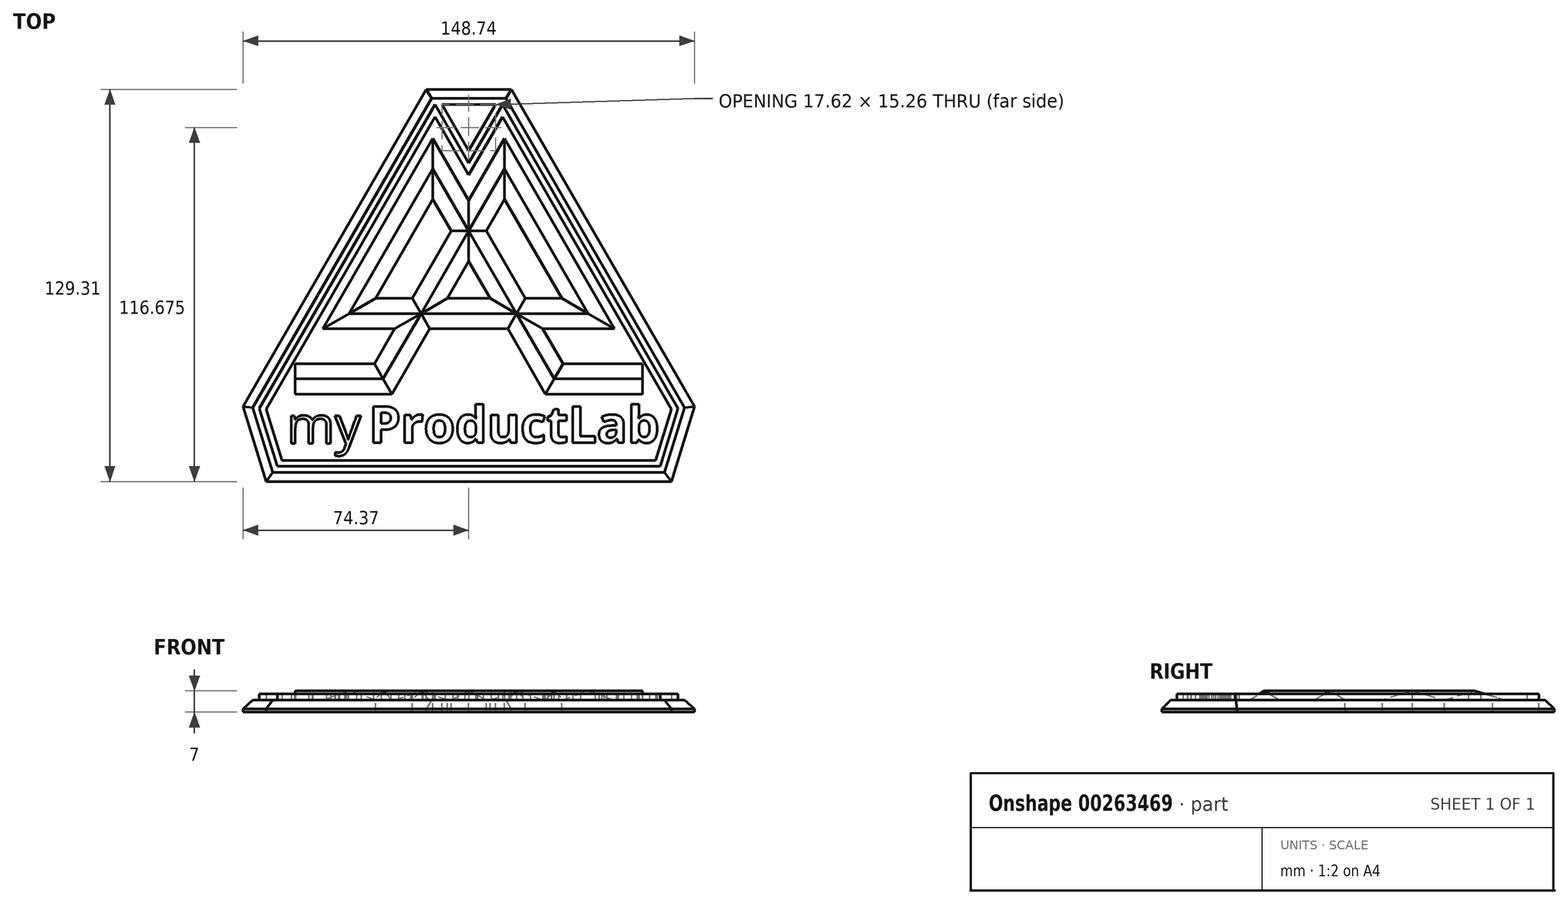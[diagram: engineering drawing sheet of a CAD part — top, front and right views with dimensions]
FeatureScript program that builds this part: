
annotation { "Feature Type Name" : "Feature", "Feature Type Description" : "" }
export const myFeature = defineFeature(function(context is Context, id is Id, definition is map)
    precondition{}
    {
        {
            var Q0;
            Q0=qCreatedBy(makeId("Top.planeOp"),FACE);
            var sketch = newSketch(context, id + "F0", { "sketchPlane" : qUnion([Q0])});
            skLineSegment(sketch, "E0", {"start": v(11.81, 20.46) * mm, "end": v(39.36, -27.25) * mm});
            skLineSegment(sketch, "E1", {"start": v(-39.36, -27.25) * mm, "end": v(-11.81, 20.46) * mm});
            skLineSegment(sketch, "E2", {"start": v(-11.81, 20.46) * mm, "end": v(28.18, -48.8) * mm});
            skLineSegment(sketch, "E3", {"start": v(28.18, -48.8) * mm, "end": v(57.26, -48.8) * mm});
            skLineSegment(sketch, "E4", {"start": v(-28.18, -48.8) * mm, "end": v(-57.26, -48.8) * mm});
            skLineSegment(sketch, "E5", {"start": v(-28.18, -48.8) * mm, "end": v(11.81, 20.46) * mm});
            skLineSegment(sketch, "E6", {"start": v(-39.36, -27.25) * mm, "end": v(0, -27.25) * mm});
            skLineSegment(sketch, "E7", {"start": v(0, -27.25) * mm, "end": v(39.36, -27.25) * mm});
            skSolve(sketch);
        }
        {
            var Q0;
            Q0=sQuery(id+"F0.wireOp",VERTEX,"E4.end");
            var Q1;
            Q1=sQuery(id+"F0.wireOp",EDGE,"E4");
            cPlane(context, id + "F1", {"entities" : qUnion([Q0, Q1]), "cplaneType" : CPlaneType.LINE_POINT, "offset" : 25 * mm, "width" : 150 * mm, "height" : 150 * mm});
        }
        {
            var Q0;
            Q0=qCreatedBy(id+"F1.planeOp",FACE);
            var sketch = newSketch(context, id + "F2", { "sketchPlane" : qUnion([Q0])});
            skLineSegment(sketch, "E8", {"start": v(48.8, 0) * mm, "end": v(43.8, -3) * mm});
            skLineSegment(sketch, "E9", {"start": v(43.8, -3) * mm, "end": v(53.8, -3) * mm});
            skLineSegment(sketch, "E10", {"start": v(53.8, -3) * mm, "end": v(48.8, 0) * mm});
            skSolve(sketch);
        }
        {
            var Q0;
            Q0 = qSketchRegion(id + "F2", true);
            var Q1;
            Q1=sQuery(id+"F0.wireOp",EDGE,"E4");
            var Q2;
            Q2=sQuery(id+"F0.wireOp",EDGE,"E5");
            var Q3;
            Q3=sQuery(id+"F0.wireOp",EDGE,"E0");
            var Q4;
            Q4=sQuery(id+"F0.wireOp",EDGE,"E7");
            sweep(context, id + "F3", {"profiles" : qUnion([Q0]), "path" : qUnion([Q1, Q2, Q3, Q4])});
        }
        {
            var Q0;
            Q0=makeQuery(id+"F3.opSweep","SWEPT_BODY",BODY,{"disambiguationData":[OSD([sQuery(id+"F0.wireOp",EDGE,"E7"),sQuery(id+"F2.wireOp",EDGE,"E8"),sQuery(id+"F2.wireOp",EDGE,"E9"),sQuery(id+"F2.wireOp",EDGE,"E10")])]});
            var Q1;
            Q1=qCreatedBy(makeId("Right.planeOp"),FACE);
            mirror(context, id + "F4", {"operationType" : NewBodyOperationType.ADD, "entities" : qUnion([Q0]), "mirrorPlane" : qUnion([Q1])});
        }
        {
            var Q0;
            {var subQ0=makeQuery(id+"F3.opSweep","SWEPT_FACE",FACE,{"disambiguationData":[OSD([sQuery(id+"F0.wireOp",EDGE,"E4"),sQuery(id+"F2.wireOp",EDGE,"E9")])]});Q0=makeQuery(id+"F4.boolean.opBoolean","MERGE",FACE,{"derivedFrom":[subQ0,makeQuery(id+"F4.opPattern","COPY",FACE,{"derivedFrom":subQ0,"instanceName":"1"})]});}
            var sketch = newSketch(context, id + "F5", { "sketchPlane" : qUnion([Q0])});
            skLineSegment(sketch, "E11", {"start": v(-74.37, 57.89) * mm, "end": v(-14, -46.67) * mm});
            skLineSegment(sketch, "E12", {"start": v(-74.37, 57.89) * mm, "end": v(-66.72, 82.64) * mm});
            skLineSegment(sketch, "E13", {"start": v(-66.72, 82.64) * mm, "end": v(0, 82.64) * mm});
            skLineSegment(sketch, "E14.MirrorCS", {"start": v(74.37, 57.89) * mm, "end": v(14, -46.67) * mm});
            skLineSegment(sketch, "E15.MirrorCS", {"start": v(74.37, 57.89) * mm, "end": v(66.72, 82.64) * mm});
            skLineSegment(sketch, "E16.MirrorCS", {"start": v(66.72, 82.64) * mm, "end": v(0, 82.64) * mm});
            skLineSegment(sketch, "E17", {"start": v(-14, -46.67) * mm, "end": v(14, -46.67) * mm});
            skPoint(sketch, "E18.orphan", {"position": v(0, -70.93) * mm});
            skSolve(sketch);
        }
        {
            var Q0;
            Q0 = qSketchRegion(id + "F5", true);
            extrude(context, id + "F6", {"entities" : qUnion([Q0]), "operationType" : NewBodyOperationType.ADD, "depth" : 4 * mm});
        }
        {
            var Q0;
            {var subQ0=sQuery(id+"F2.wireOp",EDGE,"E8");var subQ1=makeQuery(id+"F3.opSweep","SWEPT_FACE",FACE,{"disambiguationData":[OSD([sQuery(id+"F0.wireOp",EDGE,"E0"),subQ0])]});var subQ2=makeQuery(id+"F3.opSweep","SWEPT_FACE",FACE,{"disambiguationData":[OSD([sQuery(id+"F0.wireOp",EDGE,"E7"),subQ0])]});var subQ3=sQuery(id+"F0.wireOp",EDGE,"E5");var subQ4=makeQuery(id+"F3.opSweep","SWEPT_FACE",FACE,{"disambiguationData":[OSD([subQ3,subQ0])]});var subQ5=sQuery(id+"F5.wireOp",EDGE,"E11");var subQ6=sQuery(id+"F2.wireOp",EDGE,"E10");var subQ7=makeQuery(id+"F3.opSweep","SWEPT_FACE",FACE,{"disambiguationData":[OSD([subQ3,subQ6])]});var subQ8=sQuery(id+"F5.wireOp",EDGE,"E14.MirrorCS");var subQ9=makeQuery(id+"F3.opSweep","CAP_FACE",FACE,{"disambiguationData":[OSD([sQuery(id+"F0.wireOp",VERTEX,"E4.end"),subQ0,sQuery(id+"F2.wireOp",EDGE,"E9"),subQ6])],"isStart":true});var subQ10=sQuery(id+"F0.wireOp",EDGE,"E4");var subQ11=makeQuery(id+"F3.opSweep","SWEPT_FACE",FACE,{"disambiguationData":[OSD([subQ10,subQ0])]});var subQ12=makeQuery(id+"F3.opSweep","SWEPT_FACE",FACE,{"disambiguationData":[OSD([subQ10,subQ6])]});var subQ13=sQuery(id+"F5.wireOp",EDGE,"E17");var subQ14=sQuery(id+"F5.wireOp",EDGE,"E12");var subQ15=sQuery(id+"F5.wireOp",EDGE,"E16.MirrorCS");var subQ16=sQuery(id+"F5.wireOp",EDGE,"E13");var subQ17=sQuery(id+"F5.wireOp",EDGE,"E15.MirrorCS");Q0=makeQuery(id+"F6.boolean.opBoolean","SPLIT",FACE,{"disambiguationData":[TD([subQ9,subQ1,subQ11,subQ12,subQ4,subQ7,subQ2,makeQuery(id+"F4.opPattern","COPY",FACE,{"derivedFrom":subQ9,"instanceName":"1"}),makeQuery(id+"F4.opPattern","COPY",FACE,{"derivedFrom":subQ1,"instanceName":"1"}),makeQuery(id+"F4.opPattern","COPY",FACE,{"derivedFrom":subQ11,"instanceName":"1"}),makeQuery(id+"F4.opPattern","COPY",FACE,{"derivedFrom":subQ12,"instanceName":"1"}),makeQuery(id+"F4.opPattern","COPY",FACE,{"derivedFrom":subQ4,"instanceName":"1"}),makeQuery(id+"F4.opPattern","COPY",FACE,{"derivedFrom":subQ7,"instanceName":"1"}),makeQuery(id+"F4.opPattern","COPY",FACE,{"derivedFrom":subQ2,"instanceName":"1"}),makeQuery(id+"F6.opExtrude","SWEPT_FACE",FACE,{"disambiguationData":[OSD([subQ5])]}),makeQuery(id+"F6.opExtrude","SWEPT_FACE",FACE,{"disambiguationData":[OSD([subQ14])]}),makeQuery(id+"F6.opExtrude","SWEPT_FACE",FACE,{"disambiguationData":[OSD([subQ16,subQ15])]}),makeQuery(id+"F6.opExtrude","SWEPT_FACE",FACE,{"disambiguationData":[OSD([subQ8])]}),makeQuery(id+"F6.opExtrude","SWEPT_FACE",FACE,{"disambiguationData":[OSD([subQ17])]}),makeQuery(id+"F6.opExtrude","SWEPT_FACE",FACE,{"disambiguationData":[OSD([subQ13])]})])],"derivedFrom":makeQuery(id+"F6.opExtrude","CAP_FACE",FACE,{"disambiguationData":[OSD([subQ5,subQ14,subQ16,subQ8,subQ17,subQ15,subQ13])],"isStart":true})});}
            var sketch = newSketch(context, id + "F7", { "sketchPlane" : qUnion([Q0])});
            skLineSegment(sketch, "E19.0", {"start": v(-68.95, -58.5) * mm, "end": v(-11.12, 41.67) * mm});
            skLineSegment(sketch, "E19.1", {"start": v(68.95, -58.5) * mm, "end": v(11.12, 41.67) * mm});
            skLineSegment(sketch, "E19.2", {"start": v(68.95, -58.5) * mm, "end": v(63.03, -77.64) * mm});
            skLineSegment(sketch, "E19.3", {"start": v(63.03, -77.64) * mm, "end": v(-63.03, -77.64) * mm});
            skLineSegment(sketch, "E19.4", {"start": v(-68.95, -58.5) * mm, "end": v(-63.03, -77.64) * mm});
            skLineSegment(sketch, "E20", {"start": v(-11.12, 41.67) * mm, "end": v(0, 22.4) * mm});
            skLineSegment(sketch, "E21", {"start": v(0, 22.4) * mm, "end": v(11.12, 41.67) * mm});
            skLineSegment(sketch, "E22.0", {"start": v(-11.12, 37.67) * mm, "end": v(0, 18.4) * mm});
            skLineSegment(sketch, "E22.1", {"start": v(-66.78, -58.74) * mm, "end": v(-11.12, 37.67) * mm});
            skLineSegment(sketch, "E22.2", {"start": v(66.78, -58.74) * mm, "end": v(11.12, 37.67) * mm});
            skLineSegment(sketch, "E22.3", {"start": v(66.78, -58.74) * mm, "end": v(61.55, -75.64) * mm});
            skLineSegment(sketch, "E22.4", {"start": v(61.55, -75.64) * mm, "end": v(-61.55, -75.64) * mm});
            skLineSegment(sketch, "E22.5", {"start": v(0, 18.4) * mm, "end": v(11.12, 37.67) * mm});
            skLineSegment(sketch, "E22.6", {"start": v(-66.78, -58.74) * mm, "end": v(-61.55, -75.64) * mm});
            skSolve(sketch);
        }
        {
            var Q0;
            Q0 = qSketchRegion(id + "F7", true);
            extrude(context, id + "F8", {"entities" : qUnion([Q0]), "operationType" : NewBodyOperationType.ADD, "depth" : 2 * mm});
        }
        {
            var Q0;
            Q0=makeQuery(id+"F6.opExtrude","CAP_EDGE",EDGE,{"disambiguationData":[OSD([sQuery(id+"F5.wireOp",EDGE,"E17")])],"isStart":true});
            var Q1;
            Q1=makeQuery(id+"F6.opExtrude","CAP_EDGE",EDGE,{"disambiguationData":[OSD([sQuery(id+"F5.wireOp",EDGE,"E11")])],"isStart":true});
            var Q2;
            Q2=makeQuery(id+"F6.opExtrude","CAP_EDGE",EDGE,{"disambiguationData":[OSD([sQuery(id+"F5.wireOp",EDGE,"E14.MirrorCS")])],"isStart":true});
            var Q3;
            Q3=makeQuery(id+"F6.opExtrude","CAP_EDGE",EDGE,{"disambiguationData":[OSD([sQuery(id+"F5.wireOp",EDGE,"E15.MirrorCS")])],"isStart":true});
            var Q4;
            Q4=makeQuery(id+"F6.opExtrude","CAP_EDGE",EDGE,{"disambiguationData":[OSD([sQuery(id+"F5.wireOp",EDGE,"E13"),sQuery(id+"F5.wireOp",EDGE,"E16.MirrorCS")])],"isStart":true});
            var Q5;
            Q5=makeQuery(id+"F6.opExtrude","CAP_EDGE",EDGE,{"disambiguationData":[OSD([sQuery(id+"F5.wireOp",EDGE,"E12")])],"isStart":true});
            chamfer(context, id + "F9", {"entities" : qUnion([Q0, Q1, Q2, Q3, Q4, Q5]), "width" : 3 * mm, "tangentPropagation" : true});
        }
        {
            var Q0;
            {var subQ0=sQuery(id+"F5.wireOp",EDGE,"E17");var subQ1=makeQuery(id+"F6.opExtrude","SWEPT_FACE",FACE,{"disambiguationData":[OSD([subQ0])]});var subQ2=sQuery(id+"F5.wireOp",EDGE,"E15.MirrorCS");var subQ3=makeQuery(id+"F6.opExtrude","SWEPT_FACE",FACE,{"disambiguationData":[OSD([subQ2])]});var subQ4=sQuery(id+"F5.wireOp",EDGE,"E16.MirrorCS");var subQ5=sQuery(id+"F5.wireOp",EDGE,"E13");var subQ6=makeQuery(id+"F6.opExtrude","SWEPT_FACE",FACE,{"disambiguationData":[OSD([subQ5,subQ4])]});var subQ7=sQuery(id+"F5.wireOp",EDGE,"E12");var subQ8=makeQuery(id+"F6.opExtrude","SWEPT_FACE",FACE,{"disambiguationData":[OSD([subQ7])]});var subQ9=sQuery(id+"F5.wireOp",EDGE,"E11");var subQ10=makeQuery(id+"F6.opExtrude","SWEPT_FACE",FACE,{"disambiguationData":[OSD([subQ9])]});var subQ11=sQuery(id+"F5.wireOp",EDGE,"E14.MirrorCS");var subQ12=makeQuery(id+"F6.opExtrude","SWEPT_FACE",FACE,{"disambiguationData":[OSD([subQ11])]});var subQ13=sQuery(id+"F2.wireOp",EDGE,"E8");var subQ14=makeQuery(id+"F3.opSweep","SWEPT_FACE",FACE,{"disambiguationData":[OSD([sQuery(id+"F0.wireOp",EDGE,"E0"),subQ13])]});var subQ15=makeQuery(id+"F3.opSweep","SWEPT_FACE",FACE,{"disambiguationData":[OSD([sQuery(id+"F0.wireOp",EDGE,"E7"),subQ13])]});var subQ16=sQuery(id+"F0.wireOp",EDGE,"E5");var subQ17=makeQuery(id+"F3.opSweep","SWEPT_FACE",FACE,{"disambiguationData":[OSD([subQ16,subQ13])]});var subQ18=sQuery(id+"F2.wireOp",EDGE,"E10");var subQ19=makeQuery(id+"F3.opSweep","SWEPT_FACE",FACE,{"disambiguationData":[OSD([subQ16,subQ18])]});var subQ20=makeQuery(id+"F3.opSweep","CAP_FACE",FACE,{"disambiguationData":[OSD([sQuery(id+"F0.wireOp",VERTEX,"E4.end"),subQ13,sQuery(id+"F2.wireOp",EDGE,"E9"),subQ18])],"isStart":true});var subQ21=sQuery(id+"F0.wireOp",EDGE,"E4");var subQ22=makeQuery(id+"F3.opSweep","SWEPT_FACE",FACE,{"disambiguationData":[OSD([subQ21,subQ13])]});var subQ23=makeQuery(id+"F3.opSweep","SWEPT_FACE",FACE,{"disambiguationData":[OSD([subQ21,subQ18])]});Q0=makeQuery(id+"F8.boolean.opBoolean","SPLIT",FACE,{"disambiguationData":[TD([subQ10])],"derivedFrom":makeQuery(id+"F6.boolean.opBoolean","SPLIT",FACE,{"disambiguationData":[TD([subQ20,subQ14,subQ22,subQ23,subQ17,subQ19,subQ15,makeQuery(id+"F4.opPattern","COPY",FACE,{"derivedFrom":subQ20,"instanceName":"1"}),makeQuery(id+"F4.opPattern","COPY",FACE,{"derivedFrom":subQ14,"instanceName":"1"}),makeQuery(id+"F4.opPattern","COPY",FACE,{"derivedFrom":subQ22,"instanceName":"1"}),makeQuery(id+"F4.opPattern","COPY",FACE,{"derivedFrom":subQ23,"instanceName":"1"}),makeQuery(id+"F4.opPattern","COPY",FACE,{"derivedFrom":subQ17,"instanceName":"1"}),makeQuery(id+"F4.opPattern","COPY",FACE,{"derivedFrom":subQ19,"instanceName":"1"}),makeQuery(id+"F4.opPattern","COPY",FACE,{"derivedFrom":subQ15,"instanceName":"1"}),subQ10,subQ8,subQ6,subQ12,subQ3,subQ1])],"derivedFrom":makeQuery(id+"F6.opExtrude","CAP_FACE",FACE,{"disambiguationData":[OSD([subQ9,subQ7,subQ5,subQ11,subQ2,subQ4,subQ0])],"isStart":true})})});}
            var sketch = newSketch(context, id + "F10", { "sketchPlane" : qUnion([Q0])});
            skPoint(sketch, "E23", {"position": v(0, 43.67) * mm});
            skLineSegment(sketch, "E24", {"start": v(0, 26.4) * mm, "end": v(-8.81, 41.67) * mm});
            skLineSegment(sketch, "E25", {"start": v(-8.81, 41.67) * mm, "end": v(8.81, 41.67) * mm});
            skLineSegment(sketch, "E26", {"start": v(8.81, 41.67) * mm, "end": v(0, 26.4) * mm});
            skSolve(sketch);
        }
        {
            var Q0;
            Q0 = qSketchRegion(id + "F10", true);
            extrude(context, id + "F11", {"entities" : qUnion([Q0]), "operationType" : NewBodyOperationType.REMOVE, "oppositeDirection" : true, "depth" : 25 * mm});
        }
        {
            var Q0;
            {var subQ0=sQuery(id+"F2.wireOp",EDGE,"E8");var subQ1=makeQuery(id+"F3.opSweep","SWEPT_FACE",FACE,{"disambiguationData":[OSD([sQuery(id+"F0.wireOp",EDGE,"E0"),subQ0])]});var subQ2=makeQuery(id+"F4.opPattern","COPY",FACE,{"derivedFrom":subQ1,"instanceName":"1"});var subQ3=makeQuery(id+"F3.opSweep","SWEPT_FACE",FACE,{"disambiguationData":[OSD([sQuery(id+"F0.wireOp",EDGE,"E7"),subQ0])]});var subQ4=sQuery(id+"F0.wireOp",EDGE,"E5");var subQ5=makeQuery(id+"F3.opSweep","SWEPT_FACE",FACE,{"disambiguationData":[OSD([subQ4,subQ0])]});var subQ6=makeQuery(id+"F4.opPattern","COPY",FACE,{"derivedFrom":subQ5,"instanceName":"1"});var subQ7=sQuery(id+"F2.wireOp",EDGE,"E10");var subQ8=makeQuery(id+"F3.opSweep","SWEPT_FACE",FACE,{"disambiguationData":[OSD([subQ4,subQ7])]});var subQ9=makeQuery(id+"F3.opSweep","CAP_FACE",FACE,{"disambiguationData":[OSD([sQuery(id+"F0.wireOp",VERTEX,"E4.end"),subQ0,sQuery(id+"F2.wireOp",EDGE,"E9"),subQ7])],"isStart":true});var subQ10=makeQuery(id+"F4.opPattern","COPY",FACE,{"derivedFrom":subQ9,"instanceName":"1"});var subQ11=sQuery(id+"F0.wireOp",EDGE,"E4");var subQ12=makeQuery(id+"F3.opSweep","SWEPT_FACE",FACE,{"disambiguationData":[OSD([subQ11,subQ0])]});var subQ13=makeQuery(id+"F4.opPattern","COPY",FACE,{"derivedFrom":subQ12,"instanceName":"1"});var subQ14=makeQuery(id+"F3.opSweep","SWEPT_FACE",FACE,{"disambiguationData":[OSD([subQ11,subQ7])]});var subQ15=makeQuery(id+"F4.opPattern","COPY",FACE,{"derivedFrom":subQ8,"instanceName":"1"});var subQ16=makeQuery(id+"F4.opPattern","COPY",FACE,{"derivedFrom":subQ14,"instanceName":"1"});var subQ17=makeQuery(id+"F4.opPattern","COPY",FACE,{"derivedFrom":subQ3,"instanceName":"1"});var subQ18=sQuery(id+"F5.wireOp",EDGE,"E11");var subQ19=sQuery(id+"F5.wireOp",EDGE,"E14.MirrorCS");var subQ20=sQuery(id+"F5.wireOp",EDGE,"E17");var subQ21=sQuery(id+"F5.wireOp",EDGE,"E12");var subQ22=sQuery(id+"F5.wireOp",EDGE,"E16.MirrorCS");var subQ23=sQuery(id+"F5.wireOp",EDGE,"E13");var subQ24=sQuery(id+"F5.wireOp",EDGE,"E15.MirrorCS");Q0=makeQuery(id+"F8.boolean.opBoolean","SPLIT",FACE,{"disambiguationData":[TD([makeQuery(id+"F8.opExtrude","SWEPT_FACE",FACE,{"disambiguationData":[OSD([sQuery(id+"F7.wireOp",EDGE,"E22.0")])]})])],"derivedFrom":makeQuery(id+"F6.boolean.opBoolean","SPLIT",FACE,{"disambiguationData":[TD([subQ9,subQ1,subQ12,subQ14,subQ5,subQ8,subQ3,subQ10,subQ2,subQ13,subQ16,subQ6,subQ15,subQ17,makeQuery(id+"F6.opExtrude","SWEPT_FACE",FACE,{"disambiguationData":[OSD([subQ18])]}),makeQuery(id+"F6.opExtrude","SWEPT_FACE",FACE,{"disambiguationData":[OSD([subQ21])]}),makeQuery(id+"F6.opExtrude","SWEPT_FACE",FACE,{"disambiguationData":[OSD([subQ23,subQ22])]}),makeQuery(id+"F6.opExtrude","SWEPT_FACE",FACE,{"disambiguationData":[OSD([subQ19])]}),makeQuery(id+"F6.opExtrude","SWEPT_FACE",FACE,{"disambiguationData":[OSD([subQ24])]}),makeQuery(id+"F6.opExtrude","SWEPT_FACE",FACE,{"disambiguationData":[OSD([subQ20])]})])],"derivedFrom":makeQuery(id+"F6.opExtrude","CAP_FACE",FACE,{"disambiguationData":[OSD([subQ18,subQ21,subQ23,subQ19,subQ24,subQ22,subQ20])],"isStart":true})})});}
            var sketch = newSketch(context, id + "F12", { "sketchPlane" : qUnion([Q0])});
            skText(sketch, "E27", { "text": "ProductLab", "fontName": "OpenSans-Bold.ttf"});
            skText(sketch, "E28", { "text": "my", "fontName": "OpenSans-Regular.ttf"});
            const initialGuessF12  = {"E27": [-0.03287, -0.0698, 1, 0, 0.012], "E28": [-0.06, -0.07013, 1, 0, 0.01232]};
            skSetInitialGuess(sketch, initialGuessF12);
            skSolve(sketch);
        }
        {
            var Q0;
            Q0 = qSketchRegion(id + "F12", true);
            extrude(context, id + "F13", {"entities" : qUnion([Q0]), "operationType" : NewBodyOperationType.ADD, "depth" : 2 * mm});
        }
        {
            var Q0;
            {var subQ0=sQuery(id+"F2.wireOp",EDGE,"E10");var subQ1=sQuery(id+"F0.wireOp",EDGE,"E5");Q0=makeQuery(id+"F6.boolean.opBoolean","SPLIT",FACE,{"disambiguationData":[TD([makeQuery(id+"F3.opSweep","SWEPT_FACE",FACE,{"disambiguationData":[OSD([sQuery(id+"F0.wireOp",EDGE,"E0"),subQ0])]}),makeQuery(id+"F3.opSweep","SWEPT_FACE",FACE,{"disambiguationData":[OSD([subQ1,subQ0])]}),makeQuery(id+"F3.opSweep","SWEPT_FACE",FACE,{"disambiguationData":[OSD([sQuery(id+"F0.wireOp",EDGE,"E7"),subQ0])]}),makeQuery(id+"F4.opPattern","COPY",FACE,{"derivedFrom":makeQuery(id+"F3.opSweep","SWEPT_FACE",FACE,{"disambiguationData":[OSD([subQ1,sQuery(id+"F2.wireOp",EDGE,"E8")])]}),"instanceName":"1"})])],"derivedFrom":makeQuery(id+"F6.opExtrude","CAP_FACE",FACE,{"disambiguationData":[OSD([sQuery(id+"F5.wireOp",EDGE,"E11"),sQuery(id+"F5.wireOp",EDGE,"E12"),sQuery(id+"F5.wireOp",EDGE,"E13"),sQuery(id+"F5.wireOp",EDGE,"E14.MirrorCS"),sQuery(id+"F5.wireOp",EDGE,"E15.MirrorCS"),sQuery(id+"F5.wireOp",EDGE,"E16.MirrorCS"),sQuery(id+"F5.wireOp",EDGE,"E17")])],"isStart":true})});}
            var Q1;
            {var subQ0=sQuery(id+"F2.wireOp",EDGE,"E10");var subQ1=makeQuery(id+"F3.opSweep","SWEPT_FACE",FACE,{"disambiguationData":[OSD([sQuery(id+"F0.wireOp",EDGE,"E5"),subQ0])]});var subQ2=makeQuery(id+"F3.opSweep","SWEPT_FACE",FACE,{"disambiguationData":[OSD([sQuery(id+"F0.wireOp",EDGE,"E7"),subQ0])]});Q1=makeQuery(id+"F6.boolean.opBoolean","SPLIT",FACE,{"disambiguationData":[TD([subQ1,subQ2,makeQuery(id+"F4.opPattern","COPY",FACE,{"derivedFrom":subQ1,"instanceName":"1"}),makeQuery(id+"F4.opPattern","COPY",FACE,{"derivedFrom":subQ2,"instanceName":"1"})])],"derivedFrom":makeQuery(id+"F6.opExtrude","CAP_FACE",FACE,{"disambiguationData":[OSD([sQuery(id+"F5.wireOp",EDGE,"E11"),sQuery(id+"F5.wireOp",EDGE,"E12"),sQuery(id+"F5.wireOp",EDGE,"E13"),sQuery(id+"F5.wireOp",EDGE,"E14.MirrorCS"),sQuery(id+"F5.wireOp",EDGE,"E15.MirrorCS"),sQuery(id+"F5.wireOp",EDGE,"E16.MirrorCS"),sQuery(id+"F5.wireOp",EDGE,"E17")])],"isStart":true})});}
            var Q2;
            {var subQ0=sQuery(id+"F0.wireOp",EDGE,"E5");var subQ1=sQuery(id+"F2.wireOp",EDGE,"E10");Q2=makeQuery(id+"F6.boolean.opBoolean","SPLIT",FACE,{"disambiguationData":[TD([makeQuery(id+"F3.opSweep","SWEPT_FACE",FACE,{"disambiguationData":[OSD([subQ0,sQuery(id+"F2.wireOp",EDGE,"E8")])]}),makeQuery(id+"F4.opPattern","COPY",FACE,{"derivedFrom":makeQuery(id+"F3.opSweep","SWEPT_FACE",FACE,{"disambiguationData":[OSD([sQuery(id+"F0.wireOp",EDGE,"E0"),subQ1])]}),"instanceName":"1"}),makeQuery(id+"F4.opPattern","COPY",FACE,{"derivedFrom":makeQuery(id+"F3.opSweep","SWEPT_FACE",FACE,{"disambiguationData":[OSD([subQ0,subQ1])]}),"instanceName":"1"}),makeQuery(id+"F4.opPattern","COPY",FACE,{"derivedFrom":makeQuery(id+"F3.opSweep","SWEPT_FACE",FACE,{"disambiguationData":[OSD([sQuery(id+"F0.wireOp",EDGE,"E7"),subQ1])]}),"instanceName":"1"})])],"derivedFrom":makeQuery(id+"F6.opExtrude","CAP_FACE",FACE,{"disambiguationData":[OSD([sQuery(id+"F5.wireOp",EDGE,"E11"),sQuery(id+"F5.wireOp",EDGE,"E12"),sQuery(id+"F5.wireOp",EDGE,"E13"),sQuery(id+"F5.wireOp",EDGE,"E14.MirrorCS"),sQuery(id+"F5.wireOp",EDGE,"E15.MirrorCS"),sQuery(id+"F5.wireOp",EDGE,"E16.MirrorCS"),sQuery(id+"F5.wireOp",EDGE,"E17")])],"isStart":true})});}
            extrude(context, id + "F14", {"entities" : qUnion([Q0, Q1, Q2]), "operationType" : NewBodyOperationType.REMOVE, "oppositeDirection" : true, "depth" : 25 * mm});
        }
    });
